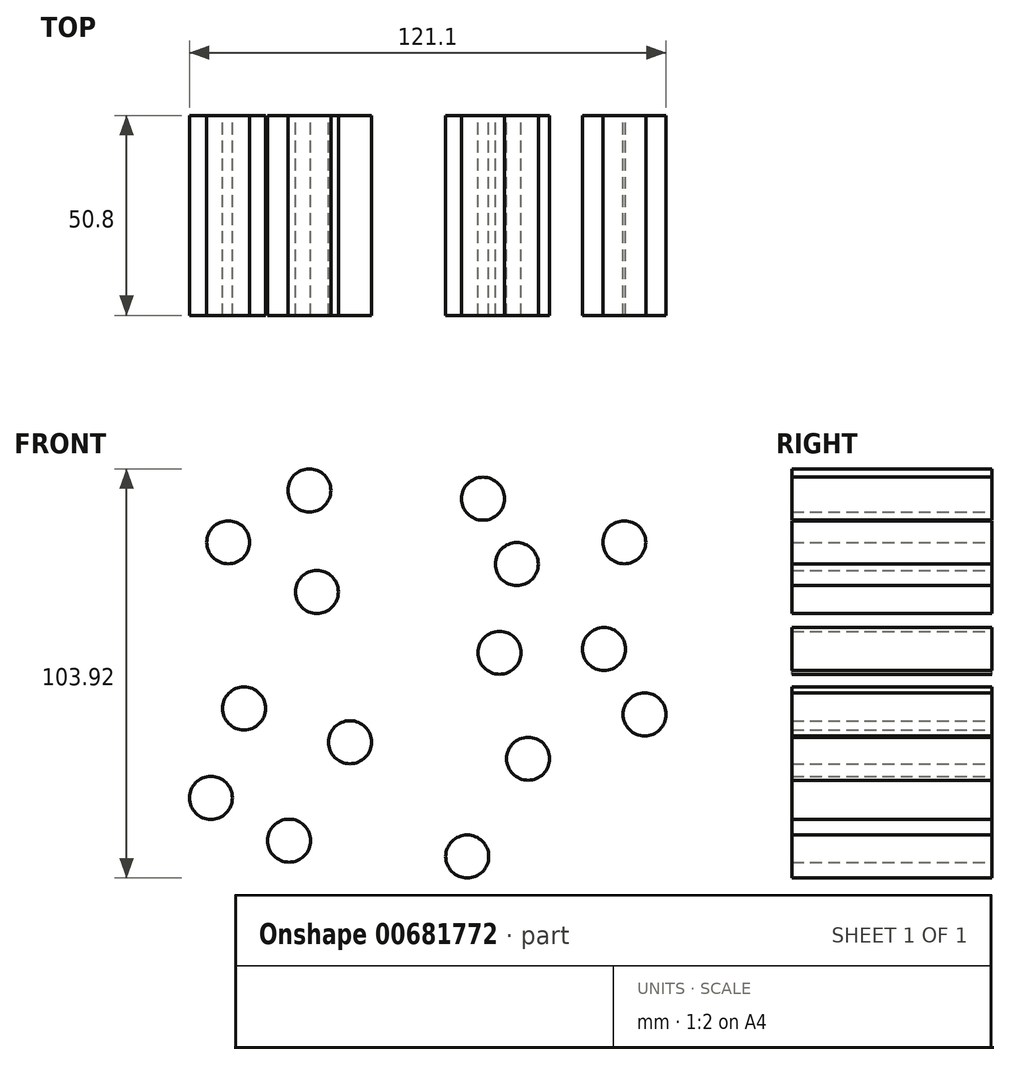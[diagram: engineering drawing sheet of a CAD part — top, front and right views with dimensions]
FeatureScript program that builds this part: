
annotation { "Feature Type Name" : "Feature", "Feature Type Description" : "" }
export const myFeature = defineFeature(function(context is Context, id is Id, definition is map)
    precondition{}
    {
        {
            var Q0;
            Q0=qCreatedBy(makeId("Front.planeOp"),FACE);
            var sketch = newSketch(context, id + "F0", { "sketchPlane" : qUnion([Q0])});
            skCircle(sketch, "E0", {"center": v(25.11, 32.18) * mm, "radius": 5.46 * mm});
            skCircle(sketch, "E1", {"center": v(16.52, 48.79) * mm, "radius": 5.46 * mm});
            skCircle(sketch, "E2", {"center": v(-27.6, 50.89) * mm, "radius": 5.46 * mm});
            skCircle(sketch, "E3", {"center": v(-25.68, 25.11) * mm, "radius": 5.46 * mm});
            skCircle(sketch, "E4", {"center": v(-48.22, 37.71) * mm, "radius": 5.46 * mm});
            skCircle(sketch, "E5", {"center": v(-17.28, -13.08) * mm, "radius": 5.46 * mm});
            skCircle(sketch, "E6", {"center": v(-44.2, -4.49) * mm, "radius": 5.46 * mm});
            skCircle(sketch, "E7", {"center": v(-32.75, -38.1) * mm, "radius": 5.46 * mm});
            skCircle(sketch, "E8", {"center": v(-52.6, -27.21) * mm, "radius": 5.46 * mm});
            skCircle(sketch, "E9", {"center": v(12.5, -42.1) * mm, "radius": 5.46 * mm});
            skCircle(sketch, "E10", {"center": v(27.97, -17.28) * mm, "radius": 5.46 * mm});
            skCircle(sketch, "E11", {"center": v(20.72, 9.64) * mm, "radius": 5.46 * mm});
            skCircle(sketch, "E12", {"center": v(47.26, 10.6) * mm, "radius": 5.46 * mm});
            skCircle(sketch, "E13", {"center": v(52.42, 37.71) * mm, "radius": 5.46 * mm});
            skCircle(sketch, "E14", {"center": v(57.57, -6.02) * mm, "radius": 5.46 * mm});
            skSolve(sketch);
        }
        {
            var Q0;
            Q0 = qSketchRegion(id + "F0", true);
            extrude(context, id + "F1", {"entities" : qUnion([Q0]), "depth" : 50.8 * mm, "offsetDistance" : 25.4 * mm});
        }
    });
